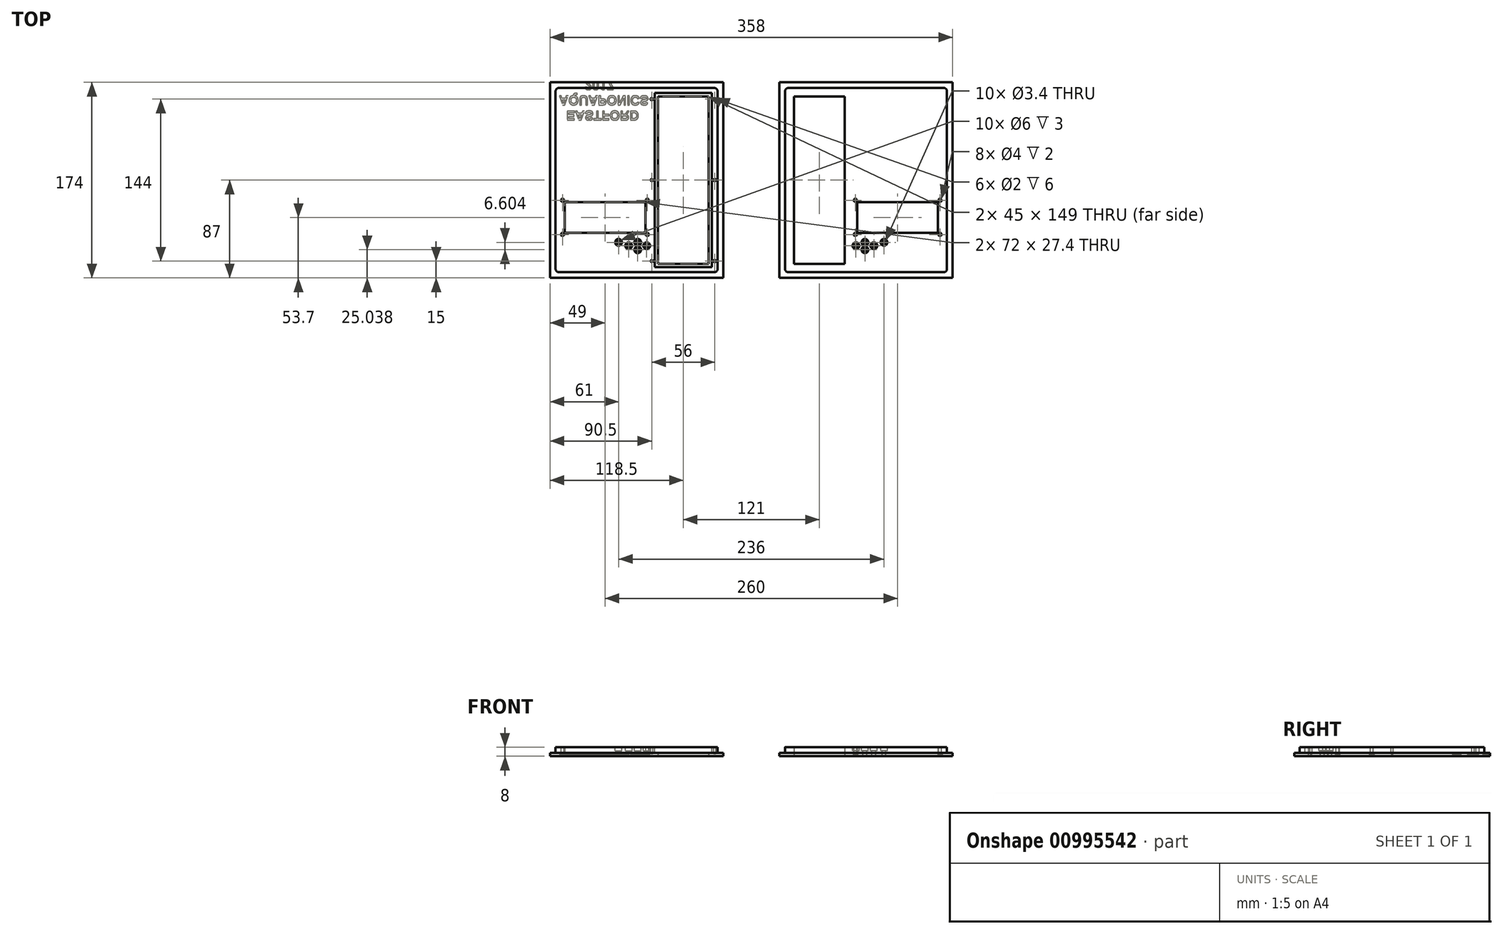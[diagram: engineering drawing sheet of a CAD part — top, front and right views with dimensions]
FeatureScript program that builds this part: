
annotation { "Feature Type Name" : "Feature", "Feature Type Description" : "" }
export const myFeature = defineFeature(function(context is Context, id is Id, definition is map)
    precondition{}
    {
        {
            var Q0;
            Q0=qCreatedBy(makeId("Top.planeOp"),FACE);
            var sketch = newSketch(context, id + "F0", { "sketchPlane" : qUnion([Q0])});
            skLineSegment(sketch, "E0.bottom", {"start": v(64, -47) * mm, "end": v(-8, -47) * mm});
            skLineSegment(sketch, "E0.top", {"start": v(64, -19.6) * mm, "end": v(-8, -19.6) * mm});
            skLineSegment(sketch, "E0.left", {"start": v(64, -47) * mm, "end": v(64, -19.6) * mm});
            skLineSegment(sketch, "E0.right", {"start": v(-8, -47) * mm, "end": v(-8, -19.6) * mm});
            skPoint(sketch, "E0.middle", {"position": v(28, -33.3) * mm});
            skLineSegment(sketch, "E1.bottom", {"start": v(72, -82) * mm, "end": v(-72, -82) * mm});
            skLineSegment(sketch, "E1.top", {"start": v(72, 82) * mm, "end": v(-72, 82) * mm});
            skLineSegment(sketch, "E1.left", {"start": v(72, -82) * mm, "end": v(72, 82) * mm});
            skLineSegment(sketch, "E1.right", {"start": v(-72, -82) * mm, "end": v(-72, 82) * mm});
            skPoint(sketch, "E1.middle", {"position": v(0, 0) * mm});
            skLineSegment(sketch, "E2.bottom", {"start": v(-64, 74.5) * mm, "end": v(-19, 74.5) * mm});
            skLineSegment(sketch, "E2.top", {"start": v(-64, -74.5) * mm, "end": v(-19, -74.5) * mm});
            skLineSegment(sketch, "E2.left", {"start": v(-64, 74.5) * mm, "end": v(-64, -74.5) * mm});
            skLineSegment(sketch, "E2.right", {"start": v(-19, 74.5) * mm, "end": v(-19, -74.5) * mm});
            skSolve(sketch);
        }
        {
            var Q0;
            Q0=makeQuery(id+"F0.imprint","IMPRINT",FACE,{"disambiguationData":[TD([[makeQuery(id+"F0.imprint","IMPRINT",EDGE,{"derivedFrom":sQuery(id+"F0.wireOp",EDGE,"E0.bottom")}),1.0]])]});
            extrude(context, id + "F1", {"entities" : qUnion([Q0]), "depth" : 5 * mm, "offsetDistance" : 25 * mm});
        }
        {
            var Q0;
            Q0=makeQuery(id+"F1.opExtrude","CAP_FACE",FACE,{"disambiguationData":[OSD([sQuery(id+"F0.wireOp",EDGE,"E0.bottom"),sQuery(id+"F0.wireOp",EDGE,"E0.top"),sQuery(id+"F0.wireOp",EDGE,"E0.left"),sQuery(id+"F0.wireOp",EDGE,"E0.right"),sQuery(id+"F0.wireOp",EDGE,"E1.bottom"),sQuery(id+"F0.wireOp",EDGE,"E1.top"),sQuery(id+"F0.wireOp",EDGE,"E1.left"),sQuery(id+"F0.wireOp",EDGE,"E1.right")])],"isStart":false});
            var sketch = newSketch(context, id + "F2", { "sketchPlane" : qUnion([Q0])});
            skCircle(sketch, "E3", {"center": v(-1, -55.36) * mm, "radius": 1.7 * mm});
            skCircle(sketch, "E4", {"center": v(-1, -61.96) * mm, "radius": 1.7 * mm});
            skCircle(sketch, "E5", {"center": v(-9, -58.4) * mm, "radius": 1.7 * mm});
            skCircle(sketch, "E6", {"center": v(7, -58.4) * mm, "radius": 1.7 * mm});
            skCircle(sketch, "E7", {"center": v(16, -55.36) * mm, "radius": 1.7 * mm});
            skCircle(sketch, "E8", {"center": v(-9.5, -48.5) * mm, "radius": 1.2 * mm});
            skCircle(sketch, "E9", {"center": v(-9.5, -18.1) * mm, "radius": 1.2 * mm});
            skCircle(sketch, "E10", {"center": v(65.8, -18.1) * mm, "radius": 1.2 * mm});
            skCircle(sketch, "E11", {"center": v(65.8, -48.5) * mm, "radius": 1.2 * mm});
            skLineSegment(sketch, "E12.bottom", {"start": v(-12.01, -65.52) * mm, "end": v(68.76, -65.52) * mm, "construction": true});
            skLineSegment(sketch, "E12.top", {"start": v(-12.01, -12.18) * mm, "end": v(68.76, -12.18) * mm, "construction": true});
            skLineSegment(sketch, "E12.left", {"start": v(-12.01, -65.52) * mm, "end": v(-12.01, -12.18) * mm, "construction": true});
            skLineSegment(sketch, "E12.right", {"start": v(68.76, -65.52) * mm, "end": v(68.76, -12.18) * mm, "construction": true});
            skSolve(sketch);
        }
        {
            var Q0;
            Q0=makeQuery(id+"F2.imprint","IMPRINT",FACE,{"disambiguationData":[TD([[makeQuery(id+"F2.imprint","IMPRINT",EDGE,{"derivedFrom":sQuery(id+"F2.wireOp",EDGE,"E5")}),1.0]])]});
            var Q1;
            Q1=makeQuery(id+"F2.imprint","IMPRINT",FACE,{"disambiguationData":[TD([[makeQuery(id+"F2.imprint","IMPRINT",EDGE,{"derivedFrom":sQuery(id+"F2.wireOp",EDGE,"E3")}),1.0]])]});
            var Q2;
            Q2=makeQuery(id+"F2.imprint","IMPRINT",FACE,{"disambiguationData":[TD([[makeQuery(id+"F2.imprint","IMPRINT",EDGE,{"derivedFrom":sQuery(id+"F2.wireOp",EDGE,"E4")}),1.0]])]});
            var Q3;
            Q3=makeQuery(id+"F2.imprint","IMPRINT",FACE,{"disambiguationData":[TD([[makeQuery(id+"F2.imprint","IMPRINT",EDGE,{"derivedFrom":sQuery(id+"F2.wireOp",EDGE,"E6")}),1.0]])]});
            var Q4;
            Q4=makeQuery(id+"F2.imprint","IMPRINT",FACE,{"disambiguationData":[TD([[makeQuery(id+"F2.imprint","IMPRINT",EDGE,{"derivedFrom":sQuery(id+"F2.wireOp",EDGE,"E7")}),1.0]])]});
            var Q5;
            Q5=makeQuery(id+"F2.imprint","IMPRINT",FACE,{"disambiguationData":[TD([[makeQuery(id+"F2.imprint","IMPRINT",EDGE,{"derivedFrom":sQuery(id+"F2.wireOp",EDGE,"E9")}),1.0]])]});
            var Q6;
            Q6=makeQuery(id+"F2.imprint","IMPRINT",FACE,{"disambiguationData":[TD([[makeQuery(id+"F2.imprint","IMPRINT",EDGE,{"derivedFrom":sQuery(id+"F2.wireOp",EDGE,"E8")}),1.0]])]});
            var Q7;
            Q7=makeQuery(id+"F2.imprint","IMPRINT",FACE,{"disambiguationData":[TD([[makeQuery(id+"F2.imprint","IMPRINT",EDGE,{"derivedFrom":sQuery(id+"F2.wireOp",EDGE,"E10")}),1.0]])]});
            var Q8;
            Q8=makeQuery(id+"F2.imprint","IMPRINT",FACE,{"disambiguationData":[TD([[makeQuery(id+"F2.imprint","IMPRINT",EDGE,{"derivedFrom":sQuery(id+"F2.wireOp",EDGE,"E11")}),1.0]])]});
            extrude(context, id + "F3", {"entities" : qUnion([Q0, Q1, Q2, Q3, Q4, Q5, Q6, Q7, Q8]), "operationType" : NewBodyOperationType.REMOVE, "oppositeDirection" : true, "depth" : 25 * mm, "offsetDistance" : 25 * mm});
        }
        {
            var Q0;
            Q0=makeQuery(id+"F1.opExtrude","CAP_FACE",FACE,{"disambiguationData":[OSD([sQuery(id+"F0.wireOp",EDGE,"E0.bottom"),sQuery(id+"F0.wireOp",EDGE,"E0.top"),sQuery(id+"F0.wireOp",EDGE,"E0.left"),sQuery(id+"F0.wireOp",EDGE,"E0.right"),sQuery(id+"F0.wireOp",EDGE,"E1.bottom"),sQuery(id+"F0.wireOp",EDGE,"E1.top"),sQuery(id+"F0.wireOp",EDGE,"E1.left"),sQuery(id+"F0.wireOp",EDGE,"E1.right"),sQuery(id+"F0.wireOp",EDGE,"E2.bottom"),sQuery(id+"F0.wireOp",EDGE,"E2.top"),sQuery(id+"F0.wireOp",EDGE,"E2.left"),sQuery(id+"F0.wireOp",EDGE,"E2.right")])],"isStart":true});
            var sketch = newSketch(context, id + "F4", { "sketchPlane" : qUnion([Q0])});
            skLineSegment(sketch, "E13.bottom", {"start": v(-77, 87) * mm, "end": v(77, 87) * mm});
            skLineSegment(sketch, "E13.top", {"start": v(-77, -87) * mm, "end": v(77, -87) * mm});
            skLineSegment(sketch, "E13.left", {"start": v(-77, 87) * mm, "end": v(-77, -87) * mm});
            skLineSegment(sketch, "E13.right", {"start": v(77, 87) * mm, "end": v(77, -87) * mm});
            skPoint(sketch, "E13.middle", {"position": v(0, 0) * mm});
            skSolve(sketch);
        }
        {
            var Q0;
            Q0=makeQuery(id+"F4.imprint","IMPRINT",FACE,{"disambiguationData":[TD([[makeQuery(id+"F4.imprint","IMPRINT",EDGE,{"derivedFrom":sQuery(id+"F4.wireOp",EDGE,"E13.bottom")}),-1.0]])]});
            var Q1;
            {var subQ6=sQuery(id+"F0.wireOp",EDGE,"E0.bottom");Q1=makeQuery(id+"F4.imprint","IMPRINT",FACE,{"disambiguationData":[TD([[makeQuery(id+"F4.imprint","IMPRINT",EDGE,{"derivedFrom":makeQuery(id+"F1.opExtrude","CAP_EDGE",EDGE,{"disambiguationData":[OSD([subQ6])],"isStart":true})}),-1.0]])]});}
            extrude(context, id + "F5", {"entities" : qUnion([Q0, Q1]), "operationType" : NewBodyOperationType.ADD, "depth" : 3 * mm, "offsetDistance" : 25 * mm});
        }
        {
            var Q0;
            Q0=makeQuery(id+"F1.opExtrude","CAP_FACE",FACE,{"disambiguationData":[OSD([sQuery(id+"F0.wireOp",EDGE,"E0.bottom"),sQuery(id+"F0.wireOp",EDGE,"E0.top"),sQuery(id+"F0.wireOp",EDGE,"E0.left"),sQuery(id+"F0.wireOp",EDGE,"E0.right"),sQuery(id+"F0.wireOp",EDGE,"E1.bottom"),sQuery(id+"F0.wireOp",EDGE,"E1.top"),sQuery(id+"F0.wireOp",EDGE,"E1.left"),sQuery(id+"F0.wireOp",EDGE,"E1.right"),sQuery(id+"F0.wireOp",EDGE,"E2.bottom"),sQuery(id+"F0.wireOp",EDGE,"E2.top"),sQuery(id+"F0.wireOp",EDGE,"E2.left"),sQuery(id+"F0.wireOp",EDGE,"E2.right")])],"isStart":false});
            var sketch = newSketch(context, id + "F6", { "sketchPlane" : qUnion([Q0])});
            skCircle(sketch, "E14", {"center": v(-1, -55.36) * mm, "radius": 3 * mm});
            skCircle(sketch, "E15", {"center": v(-1, -61.96) * mm, "radius": 3 * mm});
            skCircle(sketch, "E16", {"center": v(7, -58.4) * mm, "radius": 3 * mm});
            skCircle(sketch, "E17", {"center": v(-9, -58.4) * mm, "radius": 3 * mm});
            skCircle(sketch, "E18", {"center": v(16, -55.36) * mm, "radius": 3 * mm});
            skSolve(sketch);
        }
        {
            var Q0;
            Q0=makeQuery(id+"F6.imprint","IMPRINT",FACE,{"disambiguationData":[TD([[makeQuery(id+"F6.imprint","IMPRINT",EDGE,{"derivedFrom":sQuery(id+"F6.wireOp",EDGE,"E14")}),1.0]])]});
            var Q1;
            Q1=makeQuery(id+"F6.imprint","IMPRINT",FACE,{"disambiguationData":[TD([[makeQuery(id+"F6.imprint","IMPRINT",EDGE,{"derivedFrom":sQuery(id+"F6.wireOp",EDGE,"E15")}),1.0]])]});
            var Q2;
            Q2=makeQuery(id+"F6.imprint","IMPRINT",FACE,{"disambiguationData":[TD([[makeQuery(id+"F6.imprint","IMPRINT",EDGE,{"derivedFrom":sQuery(id+"F6.wireOp",EDGE,"E17")}),1.0]])]});
            var Q3;
            Q3=makeQuery(id+"F6.imprint","IMPRINT",FACE,{"disambiguationData":[TD([[makeQuery(id+"F6.imprint","IMPRINT",EDGE,{"derivedFrom":sQuery(id+"F6.wireOp",EDGE,"E16")}),1.0]])]});
            var Q4;
            Q4=makeQuery(id+"F6.imprint","IMPRINT",FACE,{"disambiguationData":[TD([[makeQuery(id+"F6.imprint","IMPRINT",EDGE,{"derivedFrom":sQuery(id+"F6.wireOp",EDGE,"E18")}),1.0]])]});
            extrude(context, id + "F7", {"entities" : qUnion([Q0, Q1, Q2, Q3, Q4]), "operationType" : NewBodyOperationType.REMOVE, "oppositeDirection" : true, "depth" : 3 * mm, "offsetDistance" : 25 * mm});
        }
        {
            var Q0;
            Q0=makeQuery(id+"F5.opExtrude","CAP_FACE",FACE,{"disambiguationData":[OSD([sQuery(id+"F0.wireOp",EDGE,"E0.bottom"),sQuery(id+"F0.wireOp",EDGE,"E0.top"),sQuery(id+"F0.wireOp",EDGE,"E0.left"),sQuery(id+"F0.wireOp",EDGE,"E0.right"),sQuery(id+"F0.wireOp",EDGE,"E1.bottom"),sQuery(id+"F0.wireOp",EDGE,"E1.top"),sQuery(id+"F0.wireOp",EDGE,"E1.left"),sQuery(id+"F0.wireOp",EDGE,"E1.right"),sQuery(id+"F0.wireOp",EDGE,"E2.bottom"),sQuery(id+"F0.wireOp",EDGE,"E2.top"),sQuery(id+"F0.wireOp",EDGE,"E2.left"),sQuery(id+"F0.wireOp",EDGE,"E2.right"),sQuery(id+"F2.wireOp",EDGE,"E3"),sQuery(id+"F2.wireOp",EDGE,"E4"),sQuery(id+"F2.wireOp",EDGE,"E5"),sQuery(id+"F2.wireOp",EDGE,"E6"),sQuery(id+"F2.wireOp",EDGE,"E7"),sQuery(id+"F2.wireOp",EDGE,"E8"),sQuery(id+"F2.wireOp",EDGE,"E9"),sQuery(id+"F2.wireOp",EDGE,"E10"),sQuery(id+"F2.wireOp",EDGE,"E11"),sQuery(id+"F4.wireOp",EDGE,"E13.bottom"),sQuery(id+"F4.wireOp",EDGE,"E13.top"),sQuery(id+"F4.wireOp",EDGE,"E13.left"),sQuery(id+"F4.wireOp",EDGE,"E13.right")])],"isStart":false});
            var sketch = newSketch(context, id + "F8", { "sketchPlane" : qUnion([Q0])});
            skCircle(sketch, "E19", {"center": v(-9.5, 48.5) * mm, "radius": 2 * mm});
            skCircle(sketch, "E20", {"center": v(65.8, 48.5) * mm, "radius": 2 * mm});
            skCircle(sketch, "E21", {"center": v(65.8, 18.1) * mm, "radius": 2 * mm});
            skCircle(sketch, "E22", {"center": v(-9.5, 18.1) * mm, "radius": 2 * mm});
            skSolve(sketch);
        }
        {
            var Q0;
            Q0=makeQuery(id+"F8.imprint","IMPRINT",FACE,{"disambiguationData":[TD([[makeQuery(id+"F8.imprint","IMPRINT",EDGE,{"derivedFrom":sQuery(id+"F8.wireOp",EDGE,"E19")}),1.0]])]});
            var Q1;
            Q1=makeQuery(id+"F8.imprint","IMPRINT",FACE,{"disambiguationData":[TD([[makeQuery(id+"F8.imprint","IMPRINT",EDGE,{"derivedFrom":sQuery(id+"F8.wireOp",EDGE,"E22")}),1.0]])]});
            var Q2;
            Q2=makeQuery(id+"F8.imprint","IMPRINT",FACE,{"disambiguationData":[TD([[makeQuery(id+"F8.imprint","IMPRINT",EDGE,{"derivedFrom":sQuery(id+"F8.wireOp",EDGE,"E20")}),1.0]])]});
            var Q3;
            Q3=makeQuery(id+"F8.imprint","IMPRINT",FACE,{"disambiguationData":[TD([[makeQuery(id+"F8.imprint","IMPRINT",EDGE,{"derivedFrom":sQuery(id+"F8.wireOp",EDGE,"E21")}),1.0]])]});
            extrude(context, id + "F9", {"entities" : qUnion([Q0, Q1, Q2, Q3]), "operationType" : NewBodyOperationType.REMOVE, "oppositeDirection" : true, "depth" : 2 * mm, "offsetDistance" : 25 * mm});
        }
        {
            var Q0;
            Q0=makeQuery(id+"F1.opExtrude","SWEPT_EDGE",EDGE,{"disambiguationData":[OSD([sQuery(id+"F0.wireOp",EDGE,"E1.top"),sQuery(id+"F0.wireOp",EDGE,"E1.right")])]});
            var Q1;
            Q1=makeQuery(id+"F1.opExtrude","SWEPT_EDGE",EDGE,{"disambiguationData":[OSD([sQuery(id+"F0.wireOp",EDGE,"E1.top"),sQuery(id+"F0.wireOp",EDGE,"E1.left")])]});
            var Q2;
            Q2=makeQuery(id+"F1.opExtrude","SWEPT_EDGE",EDGE,{"disambiguationData":[OSD([sQuery(id+"F0.wireOp",EDGE,"E1.bottom"),sQuery(id+"F0.wireOp",EDGE,"E1.left")])]});
            var Q3;
            Q3=makeQuery(id+"F1.opExtrude","SWEPT_EDGE",EDGE,{"disambiguationData":[OSD([sQuery(id+"F0.wireOp",EDGE,"E1.bottom"),sQuery(id+"F0.wireOp",EDGE,"E1.right")])]});
            fillet(context, id + "F10", {"entities" : qUnion([Q0, Q1, Q2, Q3]), "radius" : 3 * mm, "tangentPropagation" : true, "allowEdgeOverflow" : false});
        }
        {
            var Q0;
            Q0=makeQuery(id+"F5.opExtrude","SWEPT_FACE",FACE,{"disambiguationData":[OSD([sQuery(id+"F4.wireOp",EDGE,"E13.left")])]});
            cPlane(context, id + "F11", {"entities" : qUnion([Q0]), "cplaneType" : CPlaneType.OFFSET, "offset" : 25 * mm, "width" : 150 * mm, "height" : 150 * mm});
        }
        {
            var Q0;
            Q0=makeQuery(id+"F1.opExtrude","SWEPT_BODY",BODY,{"disambiguationData":[OSD([sQuery(id+"F0.wireOp",EDGE,"E0.bottom"),sQuery(id+"F0.wireOp",EDGE,"E0.top"),sQuery(id+"F0.wireOp",EDGE,"E0.left"),sQuery(id+"F0.wireOp",EDGE,"E0.right"),sQuery(id+"F0.wireOp",EDGE,"E1.bottom"),sQuery(id+"F0.wireOp",EDGE,"E1.top"),sQuery(id+"F0.wireOp",EDGE,"E1.left"),sQuery(id+"F0.wireOp",EDGE,"E1.right"),sQuery(id+"F0.wireOp",EDGE,"E2.bottom"),sQuery(id+"F0.wireOp",EDGE,"E2.top"),sQuery(id+"F0.wireOp",EDGE,"E2.left"),sQuery(id+"F0.wireOp",EDGE,"E2.right")])]});
            var Q1;
            Q1=qCreatedBy(id+"F11.planeOp",FACE);
            mirror(context, id + "F12", {"entities" : qUnion([Q0]), "mirrorPlane" : qUnion([Q1])});
        }
        {
            var Q0;
            Q0=makeQuery(id+"F12.opPattern","COPY",FACE,{"derivedFrom":makeQuery(id+"F1.opExtrude","CAP_FACE",FACE,{"disambiguationData":[OSD([sQuery(id+"F0.wireOp",EDGE,"E0.bottom"),sQuery(id+"F0.wireOp",EDGE,"E0.top"),sQuery(id+"F0.wireOp",EDGE,"E0.left"),sQuery(id+"F0.wireOp",EDGE,"E0.right"),sQuery(id+"F0.wireOp",EDGE,"E1.bottom"),sQuery(id+"F0.wireOp",EDGE,"E1.top"),sQuery(id+"F0.wireOp",EDGE,"E1.left"),sQuery(id+"F0.wireOp",EDGE,"E1.right"),sQuery(id+"F0.wireOp",EDGE,"E2.bottom"),sQuery(id+"F0.wireOp",EDGE,"E2.top"),sQuery(id+"F0.wireOp",EDGE,"E2.left"),sQuery(id+"F0.wireOp",EDGE,"E2.right")])],"isStart":false}),"instanceName":"1"});
            var sketch = newSketch(context, id + "F13", { "sketchPlane" : qUnion([Q0])});
            skLineSegment(sketch, "E23.bottom", {"start": v(-188, 77.5) * mm, "end": v(-137, 77.5) * mm});
            skLineSegment(sketch, "E23.top", {"start": v(-188, -77.5) * mm, "end": v(-137, -77.5) * mm});
            skLineSegment(sketch, "E23.left", {"start": v(-188, 77.5) * mm, "end": v(-188, -77.5) * mm});
            skLineSegment(sketch, "E23.right", {"start": v(-137, 77.5) * mm, "end": v(-137, -77.5) * mm});
            skSolve(sketch);
        }
        {
            var Q0;
            Q0=makeQuery(id+"F13.imprint","IMPRINT",FACE,{"disambiguationData":[TD([[makeQuery(id+"F13.imprint","IMPRINT",EDGE,{"derivedFrom":sQuery(id+"F13.wireOp",EDGE,"E23.bottom")}),-1.0]])]});
            extrude(context, id + "F14", {"entities" : qUnion([Q0]), "operationType" : NewBodyOperationType.REMOVE, "oppositeDirection" : true, "depth" : 5 * mm, "offsetDistance" : 25 * mm});
        }
        {
            var Q0;
            Q0=makeQuery(id+"F12.opPattern","COPY",FACE,{"derivedFrom":makeQuery(id+"F5.opExtrude","CAP_FACE",FACE,{"disambiguationData":[OSD([sQuery(id+"F0.wireOp",EDGE,"E0.bottom"),sQuery(id+"F0.wireOp",EDGE,"E0.top"),sQuery(id+"F0.wireOp",EDGE,"E0.left"),sQuery(id+"F0.wireOp",EDGE,"E0.right"),sQuery(id+"F0.wireOp",EDGE,"E1.bottom"),sQuery(id+"F0.wireOp",EDGE,"E1.top"),sQuery(id+"F0.wireOp",EDGE,"E1.left"),sQuery(id+"F0.wireOp",EDGE,"E1.right"),sQuery(id+"F0.wireOp",EDGE,"E2.bottom"),sQuery(id+"F0.wireOp",EDGE,"E2.top"),sQuery(id+"F0.wireOp",EDGE,"E2.left"),sQuery(id+"F0.wireOp",EDGE,"E2.right"),sQuery(id+"F2.wireOp",EDGE,"E3"),sQuery(id+"F2.wireOp",EDGE,"E4"),sQuery(id+"F2.wireOp",EDGE,"E5"),sQuery(id+"F2.wireOp",EDGE,"E6"),sQuery(id+"F2.wireOp",EDGE,"E7"),sQuery(id+"F2.wireOp",EDGE,"E8"),sQuery(id+"F2.wireOp",EDGE,"E9"),sQuery(id+"F2.wireOp",EDGE,"E10"),sQuery(id+"F2.wireOp",EDGE,"E11"),sQuery(id+"F4.wireOp",EDGE,"E13.bottom"),sQuery(id+"F4.wireOp",EDGE,"E13.top"),sQuery(id+"F4.wireOp",EDGE,"E13.left"),sQuery(id+"F4.wireOp",EDGE,"E13.right")])],"isStart":false}),"instanceName":"1"});
            var sketch = newSketch(context, id + "F15", { "sketchPlane" : qUnion([Q0])});
            skText(sketch, "E24", { "text": "  EASTFORD\nAQUAPONICS\n       2017", "fontName": "Arimo-Bold.ttf"});
            const initialGuessF15  = {"E24": [-0.273, -0.06146, 1, 0, 0.00846]};
            skSetInitialGuess(sketch, initialGuessF15);
            skSolve(sketch);
        }
        {
            var Q0;
            Q0 = qSketchRegion(id + "F15", true);
            extrude(context, id + "F16", {"entities" : qUnion([Q0]), "operationType" : NewBodyOperationType.REMOVE, "oppositeDirection" : true, "depth" : 1 * mm, "offsetDistance" : 25 * mm});
        }
        {
            var Q0;
            Q0=makeQuery(id+"F12.opPattern","COPY",FACE,{"derivedFrom":makeQuery(id+"F1.opExtrude","CAP_FACE",FACE,{"disambiguationData":[OSD([sQuery(id+"F0.wireOp",EDGE,"E0.bottom"),sQuery(id+"F0.wireOp",EDGE,"E0.top"),sQuery(id+"F0.wireOp",EDGE,"E0.left"),sQuery(id+"F0.wireOp",EDGE,"E0.right"),sQuery(id+"F0.wireOp",EDGE,"E1.bottom"),sQuery(id+"F0.wireOp",EDGE,"E1.top"),sQuery(id+"F0.wireOp",EDGE,"E1.left"),sQuery(id+"F0.wireOp",EDGE,"E1.right"),sQuery(id+"F0.wireOp",EDGE,"E2.bottom"),sQuery(id+"F0.wireOp",EDGE,"E2.top"),sQuery(id+"F0.wireOp",EDGE,"E2.left"),sQuery(id+"F0.wireOp",EDGE,"E2.right")])],"isStart":false}),"instanceName":"1"});
            var sketch = newSketch(context, id + "F17", { "sketchPlane" : qUnion([Q0])});
            skCircle(sketch, "E25", {"center": v(-190.5, 72) * mm, "radius": 1 * mm});
            skCircle(sketch, "E26", {"center": v(-134.5, 72) * mm, "radius": 1 * mm});
            skCircle(sketch, "E27", {"center": v(-190.5, -72) * mm, "radius": 1 * mm});
            skCircle(sketch, "E28", {"center": v(-134.5, -72) * mm, "radius": 1 * mm});
            skCircle(sketch, "E29", {"center": v(-190.5, 0) * mm, "radius": 1 * mm});
            skCircle(sketch, "E30", {"center": v(-134.5, 0) * mm, "radius": 1 * mm});
            skSolve(sketch);
        }
        {
            var Q0;
            Q0=makeQuery(id+"F17.imprint","IMPRINT",FACE,{"disambiguationData":[TD([[makeQuery(id+"F17.imprint","IMPRINT",EDGE,{"derivedFrom":sQuery(id+"F17.wireOp",EDGE,"E25")}),1.0]])]});
            var Q1;
            Q1=makeQuery(id+"F17.imprint","IMPRINT",FACE,{"disambiguationData":[TD([[makeQuery(id+"F17.imprint","IMPRINT",EDGE,{"derivedFrom":sQuery(id+"F17.wireOp",EDGE,"E26")}),1.0]])]});
            var Q2;
            Q2=makeQuery(id+"F17.imprint","IMPRINT",FACE,{"disambiguationData":[TD([[makeQuery(id+"F17.imprint","IMPRINT",EDGE,{"derivedFrom":sQuery(id+"F17.wireOp",EDGE,"E30")}),1.0]])]});
            var Q3;
            Q3=makeQuery(id+"F17.imprint","IMPRINT",FACE,{"disambiguationData":[TD([[makeQuery(id+"F17.imprint","IMPRINT",EDGE,{"derivedFrom":sQuery(id+"F17.wireOp",EDGE,"E29")}),1.0]])]});
            var Q4;
            Q4=makeQuery(id+"F17.imprint","IMPRINT",FACE,{"disambiguationData":[TD([[makeQuery(id+"F17.imprint","IMPRINT",EDGE,{"derivedFrom":sQuery(id+"F17.wireOp",EDGE,"E27")}),1.0]])]});
            var Q5;
            Q5=makeQuery(id+"F17.imprint","IMPRINT",FACE,{"disambiguationData":[TD([[makeQuery(id+"F17.imprint","IMPRINT",EDGE,{"derivedFrom":sQuery(id+"F17.wireOp",EDGE,"E28")}),1.0]])]});
            extrude(context, id + "F18", {"entities" : qUnion([Q0, Q1, Q2, Q3, Q4, Q5]), "operationType" : NewBodyOperationType.REMOVE, "oppositeDirection" : true, "depth" : 6 * mm, "offsetDistance" : 25 * mm});
        }
    });
